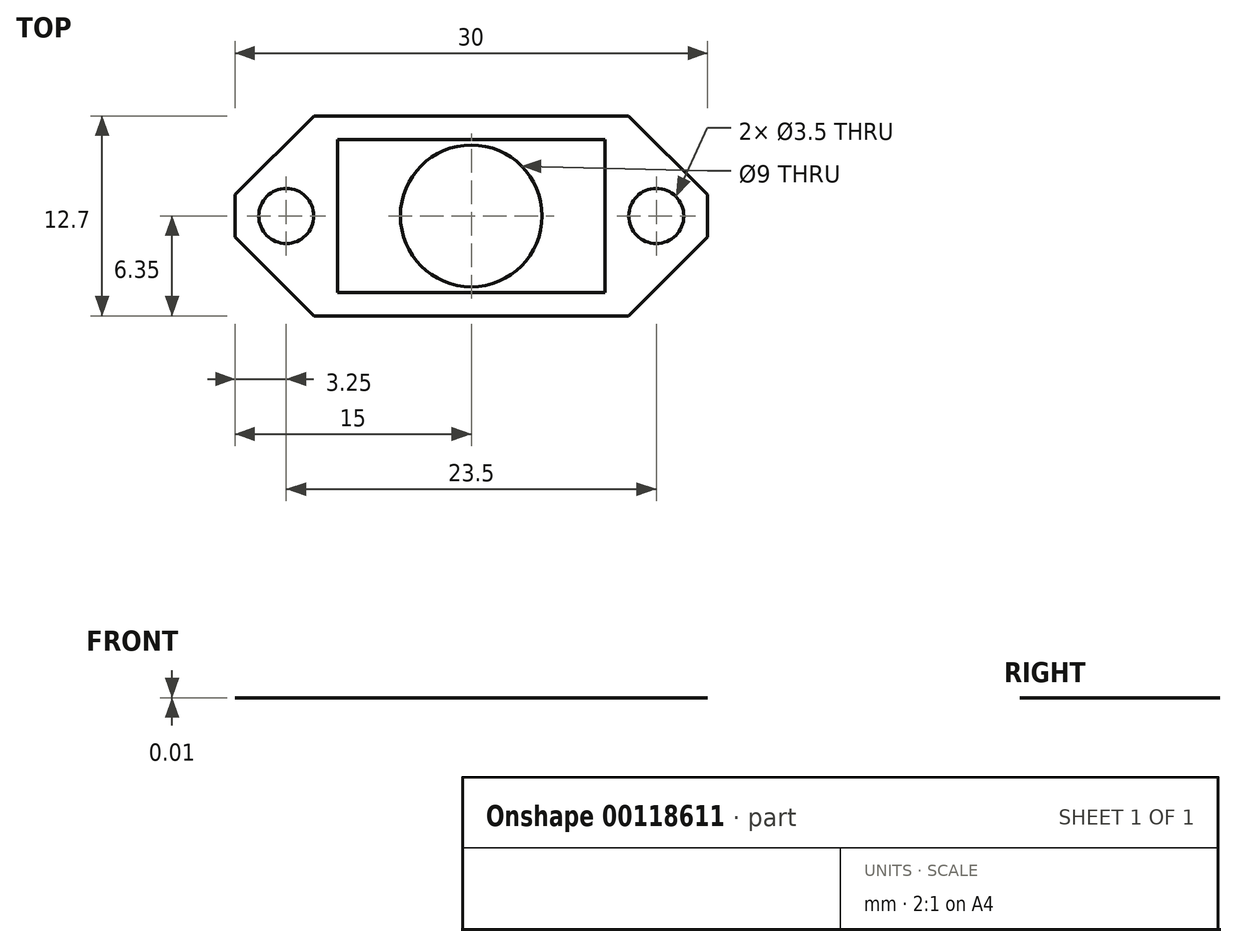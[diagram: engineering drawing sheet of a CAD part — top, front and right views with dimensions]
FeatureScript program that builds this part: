
annotation { "Feature Type Name" : "Feature", "Feature Type Description" : "" }
export const myFeature = defineFeature(function(context is Context, id is Id, definition is map)
    precondition{}
    {
        {
            var Q0;
            Q0=qCreatedBy(makeId("Top.planeOp"),FACE);
            var sketch = newSketch(context, id + "F0", { "sketchPlane" : qUnion([Q0])});
            skLineSegment(sketch, "E0.bottom", {"start": v(-15, 6.35) * mm, "end": v(15, 6.35) * mm});
            skLineSegment(sketch, "E0.top", {"start": v(-15, -6.35) * mm, "end": v(15, -6.35) * mm});
            skLineSegment(sketch, "E0.left", {"start": v(-15, 6.35) * mm, "end": v(-15, -6.35) * mm});
            skLineSegment(sketch, "E0.right", {"start": v(15, 6.35) * mm, "end": v(15, -6.35) * mm});
            skPoint(sketch, "E0.middle", {"position": v(0, 0) * mm});
            skCircle(sketch, "E1", {"center": v(-11.75, 0) * mm, "radius": 1.75 * mm});
            skCircle(sketch, "E2", {"center": v(11.75, 0) * mm, "radius": 1.75 * mm});
            skLineSegment(sketch, "E3", {"start": v(0, 6.35) * mm, "end": v(0, -6.35) * mm, "construction": true});
            skLineSegment(sketch, "E4", {"start": v(-15, 0) * mm, "end": v(15, 0) * mm, "construction": true});
            skLineSegment(sketch, "E5", {"start": v(-8.5, 4.85) * mm, "end": v(8.5, 4.85) * mm});
            skLineSegment(sketch, "E6", {"start": v(8.5, 4.85) * mm, "end": v(8.5, -4.85) * mm});
            skLineSegment(sketch, "E7", {"start": v(8.5, -4.85) * mm, "end": v(-8.5, -4.85) * mm});
            skLineSegment(sketch, "E8", {"start": v(-8.5, -4.85) * mm, "end": v(-8.5, 4.85) * mm});
            skCircle(sketch, "E9", {"center": v(0, 0) * mm, "radius": 4.5 * mm});
            skLineSegment(sketch, "E10", {"start": v(8.5, 0) * mm, "end": v(-8.5, 0) * mm, "construction": true});
            skPoint(sketch, "E11", {"position": v(0, 4.85) * mm});
            skLineSegment(sketch, "E12", {"start": v(-10, 6.35) * mm, "end": v(-15, 1.35) * mm});
            skLineSegment(sketch, "E13", {"start": v(-15, -1.35) * mm, "end": v(-10, -6.35) * mm});
            skLineSegment(sketch, "E14.MirrorCS", {"start": v(10, 6.35) * mm, "end": v(15, 1.35) * mm});
            skLineSegment(sketch, "E15.MirrorCS", {"start": v(15, -1.35) * mm, "end": v(10, -6.35) * mm});
            skLineSegment(sketch, "E16", {"start": v(-10, 6.35) * mm, "end": v(10, 6.35) * mm});
            skLineSegment(sketch, "E17", {"start": v(15, 1.35) * mm, "end": v(15, -1.35) * mm});
            skLineSegment(sketch, "E18", {"start": v(10, -6.35) * mm, "end": v(-10, -6.35) * mm});
            skLineSegment(sketch, "E19", {"start": v(-15, -1.35) * mm, "end": v(-15, 1.35) * mm});
            skSolve(sketch);
        }
        {
            var Q0;
            Q0=makeQuery(id+"F0.imprint","IMPRINT",FACE,{"disambiguationData":[TD([[makeQuery(id+"F0.imprint","IMPRINT",EDGE,{"derivedFrom":sQuery(id+"F0.wireOp",EDGE,"E1")}),-1.0]])]});
            extrude(context, id + "F1", {"entities" : qUnion([Q0]), "depth" : 1 / 101.6 * mm});
        }
        {
            var Q0;
            {var subQ0=sQuery(id+"F0.wireOp",EDGE,"E6");Q0=makeQuery(id+"F0.imprint","IMPRINT",FACE,{"disambiguationData":[TD([[makeQuery(id+"F0.imprint","IMPRINT",EDGE,{"derivedFrom":subQ0}),-1.0]])]});}
            var Q1;
            {var subQ0=sQuery(id+"F0.wireOp",EDGE,"E8");Q1=makeQuery(id+"F0.imprint","IMPRINT",FACE,{"disambiguationData":[TD([[makeQuery(id+"F0.imprint","IMPRINT",EDGE,{"derivedFrom":subQ0}),-1.0]])]});}
            extrude(context, id + "F2", {"entities" : qUnion([Q0, Q1]), "operationType" : NewBodyOperationType.ADD, "depth" : 1 / 203.2 * mm});
        }
    });
